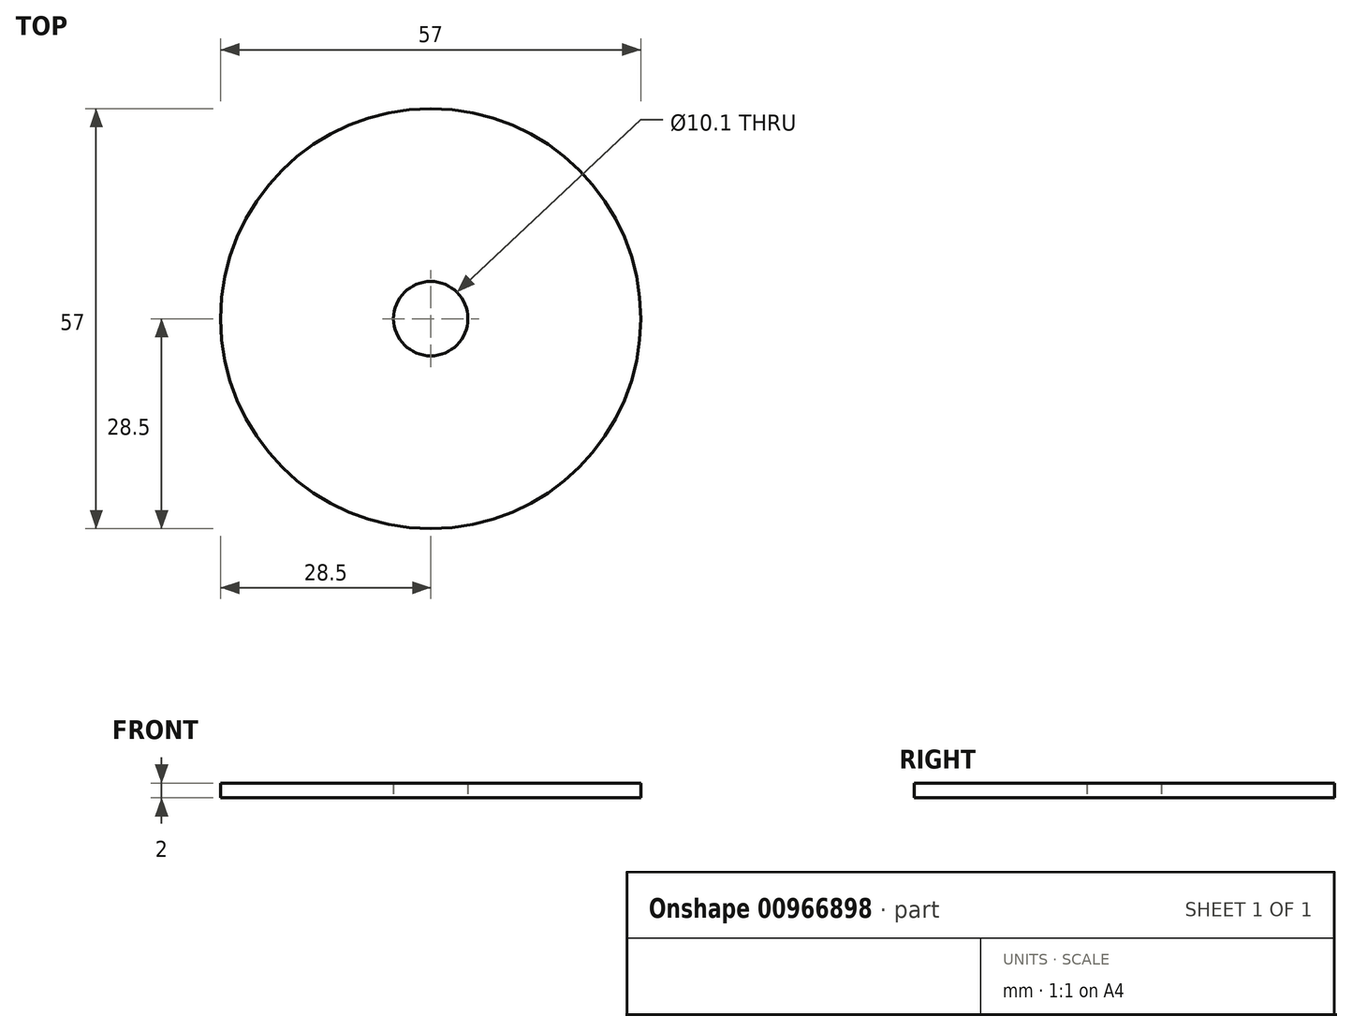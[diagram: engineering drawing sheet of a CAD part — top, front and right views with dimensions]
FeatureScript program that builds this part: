
annotation { "Feature Type Name" : "Feature", "Feature Type Description" : "" }
export const myFeature = defineFeature(function(context is Context, id is Id, definition is map)
    precondition{}
    {
        {
            var Q0;
            Q0=qCreatedBy(makeId("Top.planeOp"),FACE);
            var sketch = newSketch(context, id + "F0", { "sketchPlane" : qUnion([Q0])});
            skCircle(sketch, "E0", {"center": v(0, 0) * mm, "radius": 28.5 * mm});
            skCircle(sketch, "E1", {"center": v(0, 0) * mm, "radius": 5.05 * mm});
            skSolve(sketch);
        }
        {
            var Q0;
            Q0 = qSketchRegion(id + "F0", true);
            extrude(context, id + "F1", {"entities" : qUnion([Q0]), "depth" : 2 * mm, "offsetDistance" : 25 * mm});
        }
    });
